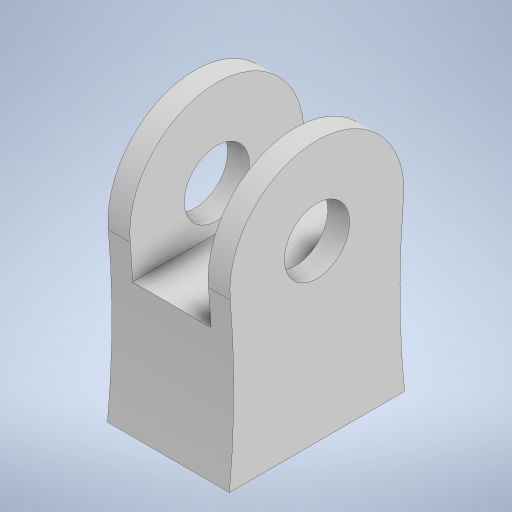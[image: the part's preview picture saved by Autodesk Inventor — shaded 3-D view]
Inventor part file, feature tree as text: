
AUTODESK INVENTOR PART (.ipt)
format: ipt  version: 2023.2 (Build 272271030, 271C)  size: 262,144 bytes
history: native  units: mm
features: extrude x4, sketch x3, plane x1, projected_geometry x1
ambient origin geometry x8: Origin, YZ Plane, XZ Plane, XY Plane, X Axis, Y Axis, Z Axis, Center Point
bodies: Solid1 (feature_tree)
feature tree (9):
  extrude  "Extrusion1"  Depth=40.0mm
  extrude  "Extrusion3"  Depth=18.0mm
  plane  "Work Plane1"
  sketch  "Sketch5"  dims[d21=10.0mm d22=0.0mm d23=0.0mm d30=40.23mm d31=40.0mm d32=200.0mm d33=200.0mm d34=438.172438mm d35=219.072282mm d36=-10.0mm d37=5.5mm d38=8.6mm d39=3.2mm d40=0.0mm d41=0.0mm d42=0.0mm]
  extrude  "Extrusion6"  TaperAngle=0.0deg  [1 undecoded]
  extrude  "Extrusion7"  Depth=3.2mm
  sketch  "Sketch1"  dims[d6=15.0mm d7=40.0mm]
  sketch  "Sketch3"  dims[d12=28.0mm d13=0.0mm d19=18.0mm]
  projected_geometry  "Projected Loop3"
note: 1 required parameter value undecoded (feature->parameter linkage not recoverable at this tier; creation-order binding heuristic only, values carry confidence <= 0.55)
